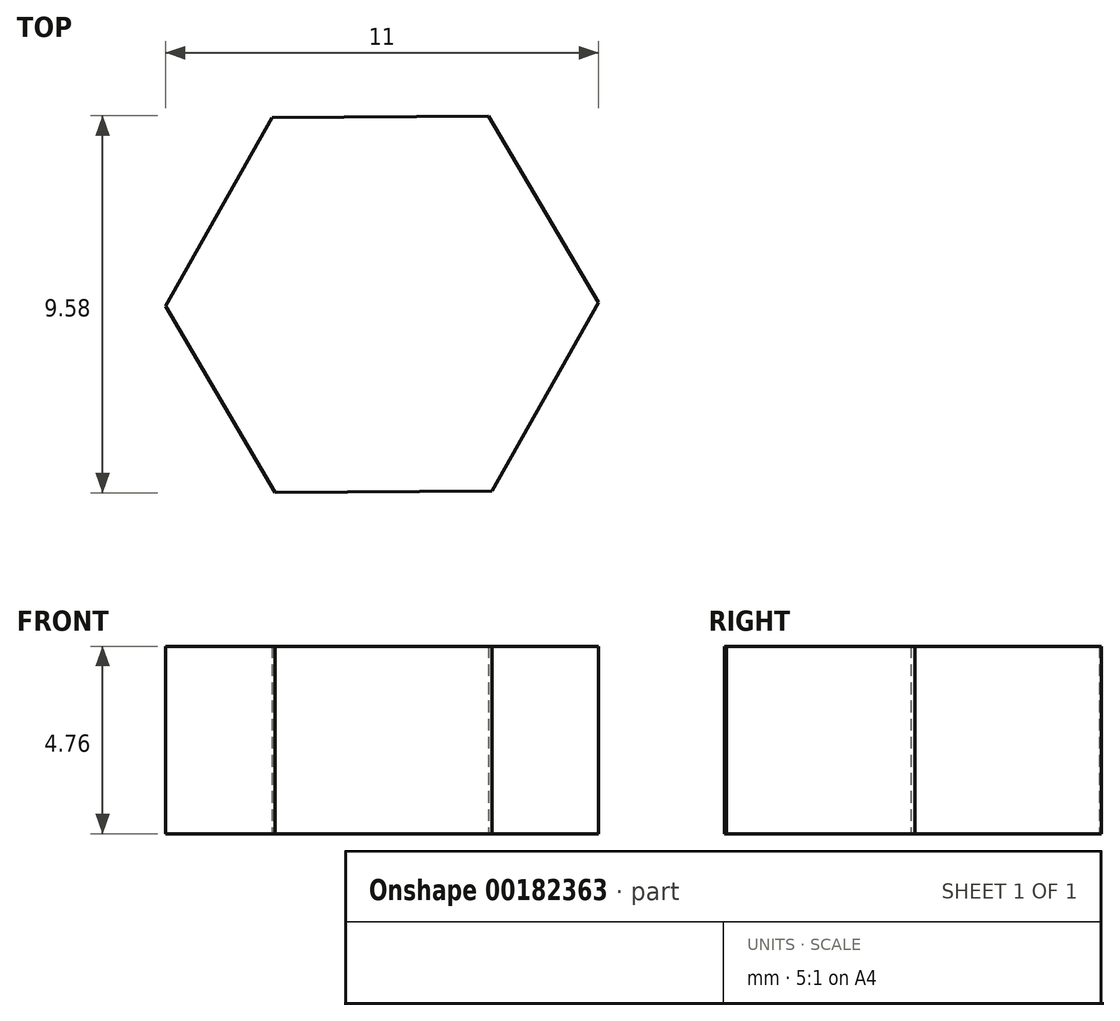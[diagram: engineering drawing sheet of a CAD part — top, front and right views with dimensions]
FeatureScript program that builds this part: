
annotation { "Feature Type Name" : "Feature", "Feature Type Description" : "" }
export const myFeature = defineFeature(function(context is Context, id is Id, definition is map)
    precondition{}
    {
        {
            var Q0;
            Q0=qCreatedBy(makeId("Top.planeOp"),FACE);
            var sketch = newSketch(context, id + "F0", { "sketchPlane" : qUnion([Q0])});
            skCircle(sketch, "E0.cCircle", {"center": v(0, 0) * mm, "radius": 4.76 * mm, "construction": true});
            skLineSegment(sketch, "E0.0", {"start": v(-5.5, -0.05) * mm, "end": v(-2.79, 4.74) * mm});
            skLineSegment(sketch, "E0.1", {"start": v(-2.79, 4.74) * mm, "end": v(2.7, 4.79) * mm});
            skLineSegment(sketch, "E0.2", {"start": v(2.7, 4.79) * mm, "end": v(5.5, 0.05) * mm});
            skLineSegment(sketch, "E0.3", {"start": v(5.5, 0.05) * mm, "end": v(2.79, -4.74) * mm});
            skLineSegment(sketch, "E0.4", {"start": v(2.79, -4.74) * mm, "end": v(-2.7, -4.79) * mm});
            skLineSegment(sketch, "E0.5", {"start": v(-2.7, -4.79) * mm, "end": v(-5.5, -0.05) * mm});
            skPoint(sketch, "E0.0.midPoint", {"position": v(-4.14, 2.35) * mm});
            skSolve(sketch);
        }
        {
            var Q0;
            Q0=qCreatedBy(makeId("Top.planeOp"),FACE);
            var sketch = newSketch(context, id + "F1", { "sketchPlane" : qUnion([Q0])});
            skCircle(sketch, "E1", {"center": v(0, 0) * mm, "radius": 1.95 * mm});
            skSolve(sketch);
        }
        {
            var Q0;
            Q0=qCreatedBy(makeId("Top.planeOp"),FACE);
            var sketch = newSketch(context, id + "F2", { "sketchPlane" : qUnion([Q0])});
            skSolve(sketch);
        }
        {
            var Q0;
            Q0 = qSketchRegion(id + "F2", true);
            var Q1;
            Q1=makeQuery(id+"F0.imprint","IMPRINT",FACE,{"disambiguationData":[TD([[makeQuery(id+"F0.imprint","IMPRINT",EDGE,{"derivedFrom":sQuery(id+"F0.wireOp",EDGE,"E0.0")}),-1.0]])]});
            extrude(context, id + "F3", {"entities" : qUnion([Q0, Q1]), "depth" : 4.76 * mm});
        }
        {
            var Q0;
            Q0=makeQuery(id+"F3.opExtrude","SWEPT_BODY",BODY,{"disambiguationData":[OSD([sQuery(id+"F0.wireOp",EDGE,"E0.0"),sQuery(id+"F0.wireOp",EDGE,"E0.1"),sQuery(id+"F0.wireOp",EDGE,"E0.2"),sQuery(id+"F0.wireOp",EDGE,"E0.3"),sQuery(id+"F0.wireOp",EDGE,"E0.4"),sQuery(id+"F0.wireOp",EDGE,"E0.5")])]});
            deleteBodies(context, id + "F4", {"entities" : qUnion([Q0])});
        }
        {
            var Q0;
            Q0=makeQuery(id+"F0.imprint","IMPRINT",FACE,{"disambiguationData":[TD([[makeQuery(id+"F0.imprint","IMPRINT",EDGE,{"derivedFrom":sQuery(id+"F0.wireOp",EDGE,"E0.0")}),-1.0]])]});
            extrude(context, id + "F5", {"entities" : qUnion([Q0]), "depth" : 4.76 * mm});
        }
        {
            var Q0;
            Q0=sQuery(id+"F1.wireOp",EDGE,"E1");
            extrude(context, id + "F6", {"bodyType" : ToolBodyType.SURFACE, "surfaceEntities" : qUnion([Q0]), "depth" : 4.76 * mm});
        }
    });
